# Revit family: BAXI_PLATINUM BC_SPLIT_iMax_iMPI-E_(UI)
name_source: partatom
category: Equipos mecánicos
units: mm (PartAtom-declared; Revit-internal decimal feet)

## family parameters
Compartido = No
Corte con vacíos al cargar = No
Cota de conector redondo = Diámetro de uso
Número OmniClass = 23.65.35.11.11
Punto de cálculo de habitación = No
Se basa en plano de trabajo = No
Siempre vertical = Sí
Tipo de pieza = Normal
Título OmniClass = Storage Water Heaters

## types (2) — shared parameters
Altura = 1003 mm  [stored 3.29068 ft]
Anchura = 457.5 mm  [stored 1.50098 ft]
BIMETRICAL = http://www.bimetrical.com
BIMETRICAL Category = Tank
Capacidad del vaso de exp. Calefacción = 10.0 L
Creado por = BIMETRICAL
D_Conector_Condensación = 32.00 mm
D_Pulgadas_CLT_Imp = 1''
D_Pulgadas_CLT_Ret = 1''
D_Pulgadas_Frig_Gas = 3/4''
D_Pulgadas_Frig_Líquido = 1/2''
Descripción = Inverter: ajusta la potencia a las necesidades de cada momento. Temperatura máxima de ida 60ºC.
Depósito de inercia: dispone de un depósito de inercia de 40 l.
Funcionamiento en cascada: suavanzada electrónica permite el control de hasta 10 bombas de calor en cascada, en modo calor y en modo frío.
Cuadro de control: la avanzada electrónica que incorpora, permite el control sobre 3 circuitos de calefacción a diferentes temperaturas, uno directo y dos con válvula mezcladora. Además,  los accesorios de regulación permiten modificar cualquier parámetro del sistema.
Conectividad: Compatible con el termostato Wi-Fi TXM BAXI Connect, tanto en calor como en frío.
Resistencias eléctricas de apoyo integradas: 4, 8 y 12 kW con alimentación trifásica.
Dext_Cu_CLT_Imp = 25.40 mm
Dext_Cu_CLT_Ret = 25.40 mm
Dext_Cu_Frig_Gas = 19.04 mm
Dext_Cu_Frig_Líquido = 12.70 mm
Diferencia máx. altura entre módulos = 30 m
Dn_Métrico_CLT_Imp = 25.00 mm
Dn_Métrico_CLT_Ret = 25.00 mm
Dn_Métrico_Frig_Gas = 20.00 mm
Dn_Métrico_Frig_Líquido = 15.00 mm
Fabricante = BAXI
Fecha de Revisión = 09/2018
Fluído frigorífico = R410A
Frecuencia = 50 Hz
IfcExportAs = IfcTankType
IfcExportType = EXPANSION
Instalación = Mural
Longitud = 600 mm
Longitud conexión frigorífica (mín/máx) = 20 m (tubo gas 3/4'') / 75 m (tubo gas de 1'')
Material principal = BAXI_Chapa
Material secundario = BAXI_Plástico
Material y Acabados = Envoltorio chapa - Tapa plástico
Nombre de tabla de consulta datos = BIBLOC iMax - Datos
Nombre de tabla de consulta referencia = BIBLOC iMax - Referencia
Número de polos = 3
Peso en vacío = 74.00 kg
Potencia acústica (dB(A)) = 43.4
Potencia acústica U. Exterior (dB(A)) = 77
Producto = Bombas de calor BIBLOC
Tarjeta electrónica para control 3r Circ. = No
Temperatura Imp. Máx. Calefacción = 60 °C
Temperatura Imp. Máx. Refrigeración = 7 °C
Tensión alimentación = 400 V
Tipo de unidad = Unidad Interior
URL = https://www.baxi.es
URL PRODUCTO = https://www.baxi.es
Versión Familia = 1.0
Versión Revit = Revit 2016 - Español

## per-type parameters (varying)
| type | C1 | Conexión frigorífica | Conjunto compatible | Intensidad máxima | Peso Fluído frigorífico |
| BC BIBLOC iMax iMPH/E 22 TR (UI) | 1 | "3/8'' - 1/4'' ó 3/8'' - 1'' | AWHP 22 TR (UE) | 19 A | 7.10 kg |
| BC BIBLOC iMax iMPH/E 27 TR (UI) | 2 | "1/2'' - 3/4'' ó 1/2'' - 1'' | AWHP 27 TR (UE) | 21 A | 7.70 kg |

note: column(s) folded — value = type name in every type: Modelo

note: [stored X ft] marks values corroborated as IEEE doubles in the binary element streams (Revit-internal decimal feet)
